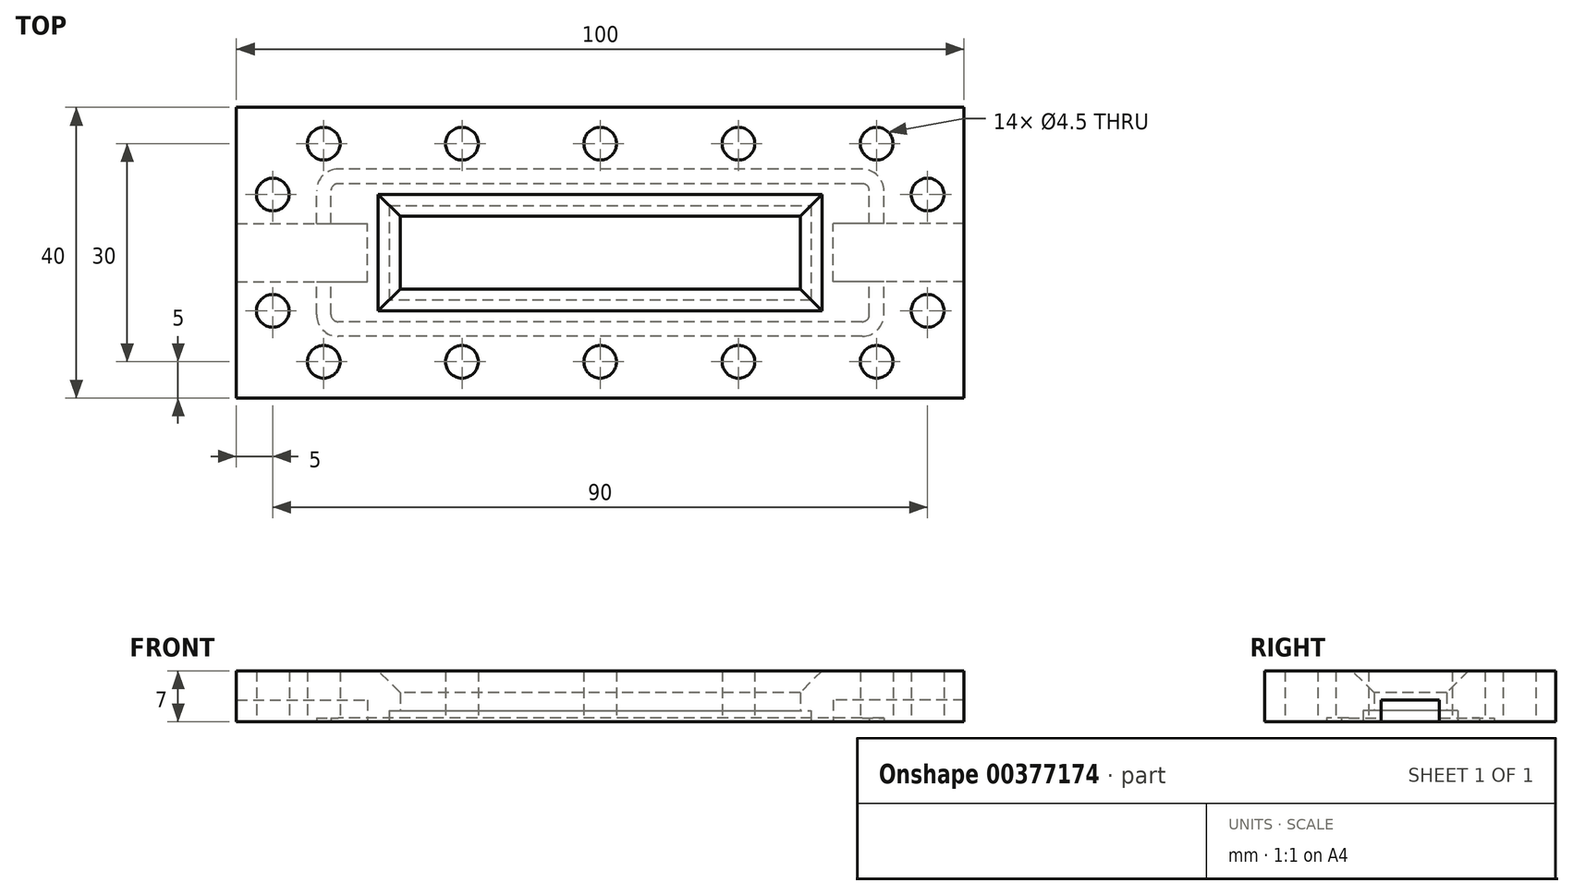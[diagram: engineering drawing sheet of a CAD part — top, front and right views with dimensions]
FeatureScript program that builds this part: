
annotation { "Feature Type Name" : "Feature", "Feature Type Description" : "" }
export const myFeature = defineFeature(function(context is Context, id is Id, definition is map)
    precondition{}
    {
        {
            var Q0;
            Q0=qCreatedBy(makeId("Top.planeOp"),FACE);
            var sketch = newSketch(context, id + "F0", { "sketchPlane" : qUnion([Q0])});
            skLineSegment(sketch, "E0.bottom", {"start": v(0, 0) * mm, "end": v(100, 0) * mm});
            skLineSegment(sketch, "E0.top", {"start": v(0, -40) * mm, "end": v(100, -40) * mm});
            skLineSegment(sketch, "E0.left", {"start": v(0, 0) * mm, "end": v(0, -40) * mm});
            skLineSegment(sketch, "E0.right", {"start": v(100, 0) * mm, "end": v(100, -40) * mm});
            skSolve(sketch);
        }
        {
            var Q0;
            Q0=makeQuery(id+"F0.imprint","IMPRINT",FACE,{"disambiguationData":[TD([[makeQuery(id+"F0.imprint","IMPRINT",EDGE,{"derivedFrom":sQuery(id+"F0.wireOp",EDGE,"E0.bottom")}),-1.0]])]});
            extrude(context, id + "F1", {"entities" : qUnion([Q0]), "depth" : 7 * mm});
        }
        {
            var Q0;
            Q0=qCreatedBy(makeId("Top.planeOp"),FACE);
            var sketch = newSketch(context, id + "F2", { "sketchPlane" : qUnion([Q0])});
            skLineSegment(sketch, "E1", {"start": v(0, 0) * mm, "end": v(0, -15) * mm});
            skLineSegment(sketch, "E2", {"start": v(0, -15) * mm, "end": v(22.5, -15) * mm});
            skLineSegment(sketch, "E3.bottom", {"start": v(22.5, -15) * mm, "end": v(77.5, -15) * mm});
            skLineSegment(sketch, "E3.top", {"start": v(22.5, -25) * mm, "end": v(77.5, -25) * mm});
            skLineSegment(sketch, "E3.left", {"start": v(22.5, -15) * mm, "end": v(22.5, -25) * mm});
            skLineSegment(sketch, "E3.right", {"start": v(77.5, -15) * mm, "end": v(77.5, -25) * mm});
            skSolve(sketch);
        }
        {
            var Q0;
            Q0=makeQuery(id+"F2.imprint","IMPRINT",FACE,{"disambiguationData":[TD([[makeQuery(id+"F2.imprint","IMPRINT",EDGE,{"derivedFrom":sQuery(id+"F2.wireOp",EDGE,"E3.bottom")}),-1.0]])]});
            extrude(context, id + "F3", {"entities" : qUnion([Q0]), "operationType" : NewBodyOperationType.REMOVE, "depth" : 8 * mm});
        }
        {
            var Q0;
            Q0=makeQuery(id+"F3.boolean.opBoolean","INTERSECT",EDGE,{"derivedFrom":[makeQuery(id+"F1.opExtrude","CAP_FACE",FACE,{"disambiguationData":[OSD([sQuery(id+"F0.wireOp",EDGE,"E0.bottom"),sQuery(id+"F0.wireOp",EDGE,"E0.top"),sQuery(id+"F0.wireOp",EDGE,"E0.left"),sQuery(id+"F0.wireOp",EDGE,"E0.right")])],"isStart":false}),makeQuery(id+"F3.opExtrude","SWEPT_FACE",FACE,{"disambiguationData":[OSD([sQuery(id+"F2.wireOp",EDGE,"E3.bottom")])]})]});
            var Q1;
            Q1=makeQuery(id+"F3.boolean.opBoolean","INTERSECT",EDGE,{"derivedFrom":[makeQuery(id+"F1.opExtrude","CAP_FACE",FACE,{"disambiguationData":[OSD([sQuery(id+"F0.wireOp",EDGE,"E0.bottom"),sQuery(id+"F0.wireOp",EDGE,"E0.top"),sQuery(id+"F0.wireOp",EDGE,"E0.left"),sQuery(id+"F0.wireOp",EDGE,"E0.right")])],"isStart":false}),makeQuery(id+"F3.opExtrude","SWEPT_FACE",FACE,{"disambiguationData":[OSD([sQuery(id+"F2.wireOp",EDGE,"E3.left")])]})]});
            var Q2;
            Q2=makeQuery(id+"F3.boolean.opBoolean","INTERSECT",EDGE,{"derivedFrom":[makeQuery(id+"F1.opExtrude","CAP_FACE",FACE,{"disambiguationData":[OSD([sQuery(id+"F0.wireOp",EDGE,"E0.bottom"),sQuery(id+"F0.wireOp",EDGE,"E0.top"),sQuery(id+"F0.wireOp",EDGE,"E0.left"),sQuery(id+"F0.wireOp",EDGE,"E0.right")])],"isStart":false}),makeQuery(id+"F3.opExtrude","SWEPT_FACE",FACE,{"disambiguationData":[OSD([sQuery(id+"F2.wireOp",EDGE,"E3.top")])]})]});
            var Q3;
            Q3=makeQuery(id+"F3.boolean.opBoolean","INTERSECT",EDGE,{"derivedFrom":[makeQuery(id+"F1.opExtrude","CAP_FACE",FACE,{"disambiguationData":[OSD([sQuery(id+"F0.wireOp",EDGE,"E0.bottom"),sQuery(id+"F0.wireOp",EDGE,"E0.top"),sQuery(id+"F0.wireOp",EDGE,"E0.left"),sQuery(id+"F0.wireOp",EDGE,"E0.right")])],"isStart":false}),makeQuery(id+"F3.opExtrude","SWEPT_FACE",FACE,{"disambiguationData":[OSD([sQuery(id+"F2.wireOp",EDGE,"E3.right")])]})]});
            chamfer(context, id + "F4", {"entities" : qUnion([Q0, Q1, Q2, Q3]), "width" : 3 * mm, "tangentPropagation" : true});
        }
        {
            var Q0;
            Q0=qCreatedBy(makeId("Top.planeOp"),FACE);
            var sketch = newSketch(context, id + "F5", { "sketchPlane" : qUnion([Q0])});
            skCircle(sketch, "E4", {"center": v(5, -12) * mm, "radius": 2.25 * mm});
            skCircle(sketch, "E5", {"center": v(5, -28) * mm, "radius": 2.25 * mm});
            skCircle(sketch, "E6", {"center": v(12, -5) * mm, "radius": 2.25 * mm});
            skCircle(sketch, "E7", {"center": v(12, -35) * mm, "radius": 2.25 * mm});
            skCircle(sketch, "E8", {"center": v(31, -35) * mm, "radius": 2.25 * mm});
            skCircle(sketch, "E9", {"center": v(50, -35) * mm, "radius": 2.25 * mm});
            skCircle(sketch, "E10", {"center": v(69, -35) * mm, "radius": 2.25 * mm});
            skCircle(sketch, "E11", {"center": v(88, -35) * mm, "radius": 2.25 * mm});
            skCircle(sketch, "E12", {"center": v(95, -28) * mm, "radius": 2.25 * mm});
            skCircle(sketch, "E13", {"center": v(95, -12) * mm, "radius": 2.25 * mm});
            skCircle(sketch, "E14", {"center": v(88, -5) * mm, "radius": 2.25 * mm});
            skCircle(sketch, "E15", {"center": v(69, -5) * mm, "radius": 2.25 * mm});
            skCircle(sketch, "E16", {"center": v(50, -5) * mm, "radius": 2.25 * mm});
            skCircle(sketch, "E17", {"center": v(31, -5) * mm, "radius": 2.25 * mm});
            skSolve(sketch);
        }
        {
            var Q0;
            Q0=makeQuery(id+"F5.imprint","IMPRINT",FACE,{"disambiguationData":[TD([[makeQuery(id+"F5.imprint","IMPRINT",EDGE,{"derivedFrom":sQuery(id+"F5.wireOp",EDGE,"E7")}),1.0]])]});
            var Q1;
            Q1=makeQuery(id+"F5.imprint","IMPRINT",FACE,{"disambiguationData":[TD([[makeQuery(id+"F5.imprint","IMPRINT",EDGE,{"derivedFrom":sQuery(id+"F5.wireOp",EDGE,"E8")}),1.0]])]});
            var Q2;
            Q2=makeQuery(id+"F5.imprint","IMPRINT",FACE,{"disambiguationData":[TD([[makeQuery(id+"F5.imprint","IMPRINT",EDGE,{"derivedFrom":sQuery(id+"F5.wireOp",EDGE,"E9")}),1.0]])]});
            var Q3;
            Q3=makeQuery(id+"F5.imprint","IMPRINT",FACE,{"disambiguationData":[TD([[makeQuery(id+"F5.imprint","IMPRINT",EDGE,{"derivedFrom":sQuery(id+"F5.wireOp",EDGE,"E10")}),1.0]])]});
            var Q4;
            Q4=makeQuery(id+"F5.imprint","IMPRINT",FACE,{"disambiguationData":[TD([[makeQuery(id+"F5.imprint","IMPRINT",EDGE,{"derivedFrom":sQuery(id+"F5.wireOp",EDGE,"E11")}),1.0]])]});
            var Q5;
            Q5=makeQuery(id+"F5.imprint","IMPRINT",FACE,{"disambiguationData":[TD([[makeQuery(id+"F5.imprint","IMPRINT",EDGE,{"derivedFrom":sQuery(id+"F5.wireOp",EDGE,"E12")}),1.0]])]});
            var Q6;
            Q6=makeQuery(id+"F5.imprint","IMPRINT",FACE,{"disambiguationData":[TD([[makeQuery(id+"F5.imprint","IMPRINT",EDGE,{"derivedFrom":sQuery(id+"F5.wireOp",EDGE,"E13")}),1.0]])]});
            var Q7;
            Q7=makeQuery(id+"F5.imprint","IMPRINT",FACE,{"disambiguationData":[TD([[makeQuery(id+"F5.imprint","IMPRINT",EDGE,{"derivedFrom":sQuery(id+"F5.wireOp",EDGE,"E14")}),1.0]])]});
            var Q8;
            Q8=makeQuery(id+"F5.imprint","IMPRINT",FACE,{"disambiguationData":[TD([[makeQuery(id+"F5.imprint","IMPRINT",EDGE,{"derivedFrom":sQuery(id+"F5.wireOp",EDGE,"E15")}),1.0]])]});
            var Q9;
            Q9=makeQuery(id+"F5.imprint","IMPRINT",FACE,{"disambiguationData":[TD([[makeQuery(id+"F5.imprint","IMPRINT",EDGE,{"derivedFrom":sQuery(id+"F5.wireOp",EDGE,"E16")}),1.0]])]});
            var Q10;
            Q10=makeQuery(id+"F5.imprint","IMPRINT",FACE,{"disambiguationData":[TD([[makeQuery(id+"F5.imprint","IMPRINT",EDGE,{"derivedFrom":sQuery(id+"F5.wireOp",EDGE,"E17")}),1.0]])]});
            var Q11;
            Q11=makeQuery(id+"F5.imprint","IMPRINT",FACE,{"disambiguationData":[TD([[makeQuery(id+"F5.imprint","IMPRINT",EDGE,{"derivedFrom":sQuery(id+"F5.wireOp",EDGE,"E6")}),1.0]])]});
            var Q12;
            Q12=makeQuery(id+"F5.imprint","IMPRINT",FACE,{"disambiguationData":[TD([[makeQuery(id+"F5.imprint","IMPRINT",EDGE,{"derivedFrom":sQuery(id+"F5.wireOp",EDGE,"E4")}),1.0]])]});
            var Q13;
            Q13=makeQuery(id+"F5.imprint","IMPRINT",FACE,{"disambiguationData":[TD([[makeQuery(id+"F5.imprint","IMPRINT",EDGE,{"derivedFrom":sQuery(id+"F5.wireOp",EDGE,"E5")}),1.0]])]});
            extrude(context, id + "F6", {"entities" : qUnion([Q0, Q1, Q2, Q3, Q4, Q5, Q6, Q7, Q8, Q9, Q10, Q11, Q12, Q13]), "operationType" : NewBodyOperationType.REMOVE, "depth" : 18.9 * mm});
        }
        {
            var Q0;
            Q0=makeQuery(id+"F1.opExtrude","CAP_FACE",FACE,{"disambiguationData":[OSD([sQuery(id+"F0.wireOp",EDGE,"E0.bottom"),sQuery(id+"F0.wireOp",EDGE,"E0.top"),sQuery(id+"F0.wireOp",EDGE,"E0.left"),sQuery(id+"F0.wireOp",EDGE,"E0.right")])],"isStart":true});
            var sketch = newSketch(context, id + "F7", { "sketchPlane" : qUnion([Q0])});
            skLineSegment(sketch, "E18", {"start": v(0, 40) * mm, "end": v(0, 24) * mm});
            skLineSegment(sketch, "E19.bottom", {"start": v(0, 24) * mm, "end": v(18, 24) * mm});
            skLineSegment(sketch, "E19.top", {"start": v(0, 16) * mm, "end": v(18, 16) * mm});
            skLineSegment(sketch, "E19.left", {"start": v(0, 24) * mm, "end": v(0, 16) * mm});
            skLineSegment(sketch, "E19.right", {"start": v(18, 24) * mm, "end": v(18, 16) * mm});
            skLineSegment(sketch, "E20", {"start": v(100, 40) * mm, "end": v(100, 24) * mm});
            skLineSegment(sketch, "E21.bottom", {"start": v(100, 24) * mm, "end": v(82, 24) * mm});
            skLineSegment(sketch, "E21.top", {"start": v(100, 16) * mm, "end": v(82, 16) * mm});
            skLineSegment(sketch, "E21.left", {"start": v(100, 24) * mm, "end": v(100, 16) * mm});
            skLineSegment(sketch, "E21.right", {"start": v(82, 24) * mm, "end": v(82, 16) * mm});
            skSolve(sketch);
        }
        {
            var Q0;
            Q0=makeQuery(id+"F7.imprint","IMPRINT",FACE,{"disambiguationData":[TD([[makeQuery(id+"F7.imprint","IMPRINT",EDGE,{"derivedFrom":sQuery(id+"F7.wireOp",EDGE,"E19.bottom")}),-1.0]])]});
            var Q1;
            Q1=makeQuery(id+"F7.imprint","IMPRINT",FACE,{"disambiguationData":[TD([[makeQuery(id+"F7.imprint","IMPRINT",EDGE,{"derivedFrom":sQuery(id+"F7.wireOp",EDGE,"E21.bottom")}),1.0]])]});
            extrude(context, id + "F8", {"entities" : qUnion([Q0, Q1]), "operationType" : NewBodyOperationType.REMOVE, "oppositeDirection" : true, "depth" : 3 * mm});
        }
        {
            var Q0;
            Q0=makeQuery(id+"F1.opExtrude","CAP_FACE",FACE,{"disambiguationData":[OSD([sQuery(id+"F0.wireOp",EDGE,"E0.bottom"),sQuery(id+"F0.wireOp",EDGE,"E0.top"),sQuery(id+"F0.wireOp",EDGE,"E0.left"),sQuery(id+"F0.wireOp",EDGE,"E0.right")])],"isStart":true});
            var sketch = newSketch(context, id + "F9", { "sketchPlane" : qUnion([Q0])});
            skLineSegment(sketch, "E22", {"start": v(77.5, 13.5) * mm, "end": v(79, 13.5) * mm});
            skLineSegment(sketch, "E23.bottom", {"start": v(79, 13.5) * mm, "end": v(21, 13.5) * mm});
            skLineSegment(sketch, "E23.top", {"start": v(79, 26.5) * mm, "end": v(21, 26.5) * mm});
            skLineSegment(sketch, "E23.left", {"start": v(79, 13.5) * mm, "end": v(79, 26.5) * mm});
            skLineSegment(sketch, "E23.right", {"start": v(21, 13.5) * mm, "end": v(21, 26.5) * mm});
            skSolve(sketch);
        }
        {
            var Q0;
            Q0=makeQuery(id+"F9.imprint","IMPRINT",FACE,{"disambiguationData":[TD([[makeQuery(id+"F9.imprint","IMPRINT",EDGE,{"derivedFrom":sQuery(id+"F9.wireOp",EDGE,"55d1Z3Bj-iSyF-8nKf-xETa-EfIaiZM0lU5P.top")}),1.0]])]});
            var Q1;
            Q1=makeQuery(id+"F9.imprint","IMPRINT",FACE,{"disambiguationData":[TD([[makeQuery(id+"F9.imprint","IMPRINT",EDGE,{"derivedFrom":sQuery(id+"F9.wireOp",EDGE,"E23.top")}),1.0]])]});
            extrude(context, id + "F10", {"entities" : qUnion([Q0, Q1]), "operationType" : NewBodyOperationType.REMOVE, "oppositeDirection" : true, "depth" : 1.5 * mm});
        }
        {
            var Q0;
            Q0=makeQuery(id+"F1.opExtrude","CAP_FACE",FACE,{"disambiguationData":[OSD([sQuery(id+"F0.wireOp",EDGE,"E0.bottom"),sQuery(id+"F0.wireOp",EDGE,"E0.top"),sQuery(id+"F0.wireOp",EDGE,"E0.left"),sQuery(id+"F0.wireOp",EDGE,"E0.right")])],"isStart":true});
            var sketch = newSketch(context, id + "F11", { "sketchPlane" : qUnion([Q0])});
            skLineSegment(sketch, "E24.top", {"start": v(16, 8.5) * mm, "end": v(84, 8.5) * mm});
            skLineSegment(sketch, "E24.left", {"start": v(13, 28.5) * mm, "end": v(13, 11.5) * mm});
            skLineSegment(sketch, "E24.right", {"start": v(87, 28.5) * mm, "end": v(87, 11.5) * mm});
            skLineSegment(sketch, "E25.bottom", {"start": v(16, 29.5) * mm, "end": v(84, 29.5) * mm});
            skLineSegment(sketch, "E25.top", {"start": v(16, 10.5) * mm, "end": v(84, 10.5) * mm});
            skPoint(sketch, "E26.visualSharp", {"position": v(15, 29.5) * mm});
            skPoint(sketch, "E27.visualSharp", {"position": v(85, 29.5) * mm});
            skPoint(sketch, "E28.visualSharp", {"position": v(15, 10.5) * mm});
            skLineSegment(sketch, "E29", {"start": v(16, 31.5) * mm, "end": v(84, 31.5) * mm});
            skLineSegment(sketch, "E30.bottom", {"start": v(86, 31.5) * mm, "end": v(14, 31.5) * mm});
            skLineSegment(sketch, "E30.top", {"start": v(86, 8.5) * mm, "end": v(14, 8.5) * mm});
            skLineSegment(sketch, "E30.left", {"start": v(89, 28.5) * mm, "end": v(89, 11.5) * mm});
            skLineSegment(sketch, "E30.right", {"start": v(11, 28.5) * mm, "end": v(11, 11.5) * mm});
            skLineSegment(sketch, "E31.bottom", {"start": v(86, 29.5) * mm, "end": v(14, 29.5) * mm});
            skLineSegment(sketch, "E31.top", {"start": v(86, 10.5) * mm, "end": v(14, 10.5) * mm});
            skPoint(sketch, "E32.visualSharp", {"position": v(87, 29.5) * mm});
            skArc(sketch, "E32.filletArc", {"start": v(87, 28.5) * mm, "mid": v(86.7, 29.2) * mm, "end": v(86, 29.5) * mm});
            skPoint(sketch, "E33.visualSharp", {"position": v(13, 29.5) * mm});
            skArc(sketch, "E33.filletArc", {"start": v(14, 29.5) * mm, "mid": v(13.3, 29.2) * mm, "end": v(13, 28.5) * mm});
            skPoint(sketch, "E34.visualSharp", {"position": v(13, 10.5) * mm});
            skArc(sketch, "E34.filletArc", {"start": v(13, 11.5) * mm, "mid": v(13.3, 10.8) * mm, "end": v(14, 10.5) * mm});
            skPoint(sketch, "E35.visualSharp", {"position": v(87, 10.5) * mm});
            skArc(sketch, "E35.filletArc", {"start": v(86, 10.5) * mm, "mid": v(86.7, 10.8) * mm, "end": v(87, 11.5) * mm});
            skPoint(sketch, "E36.visualSharp", {"position": v(89, 8.5) * mm});
            skArc(sketch, "E36.filletArc", {"start": v(86, 8.5) * mm, "mid": v(88.12, 9.38) * mm, "end": v(89, 11.5) * mm});
            skArc(sketch, "E37.filletArc", {"start": v(11, 11.5) * mm, "mid": v(11.88, 9.38) * mm, "end": v(14, 8.5) * mm});
            skArc(sketch, "E38.filletArc", {"start": v(14, 31.5) * mm, "mid": v(11.88, 30.62) * mm, "end": v(11, 28.5) * mm});
            skArc(sketch, "E39.filletArc", {"start": v(89, 28.5) * mm, "mid": v(88.12, 30.62) * mm, "end": v(86, 31.5) * mm});
            skSolve(sketch);
        }
        {
            var Q0;
            {var subQ0=sQuery(id+"F11.wireOp",EDGE,"E34.filletArc");Q0=makeQuery(id+"F11.imprint","IMPRINT",FACE,{"disambiguationData":[TD([[makeQuery(id+"F11.imprint","IMPRINT",EDGE,{"derivedFrom":subQ0}),-1.0]])]});}
            var Q1;
            {var subQ4=sQuery(id+"F11.wireOp",EDGE,"E32.filletArc");Q1=makeQuery(id+"F11.imprint","IMPRINT",FACE,{"disambiguationData":[TD([[makeQuery(id+"F11.imprint","IMPRINT",EDGE,{"derivedFrom":subQ4}),-1.0]])]});}
            extrude(context, id + "F12", {"entities" : qUnion([Q0, Q1]), "operationType" : NewBodyOperationType.REMOVE, "oppositeDirection" : true, "depth" : 0.5 * mm});
        }
    });
